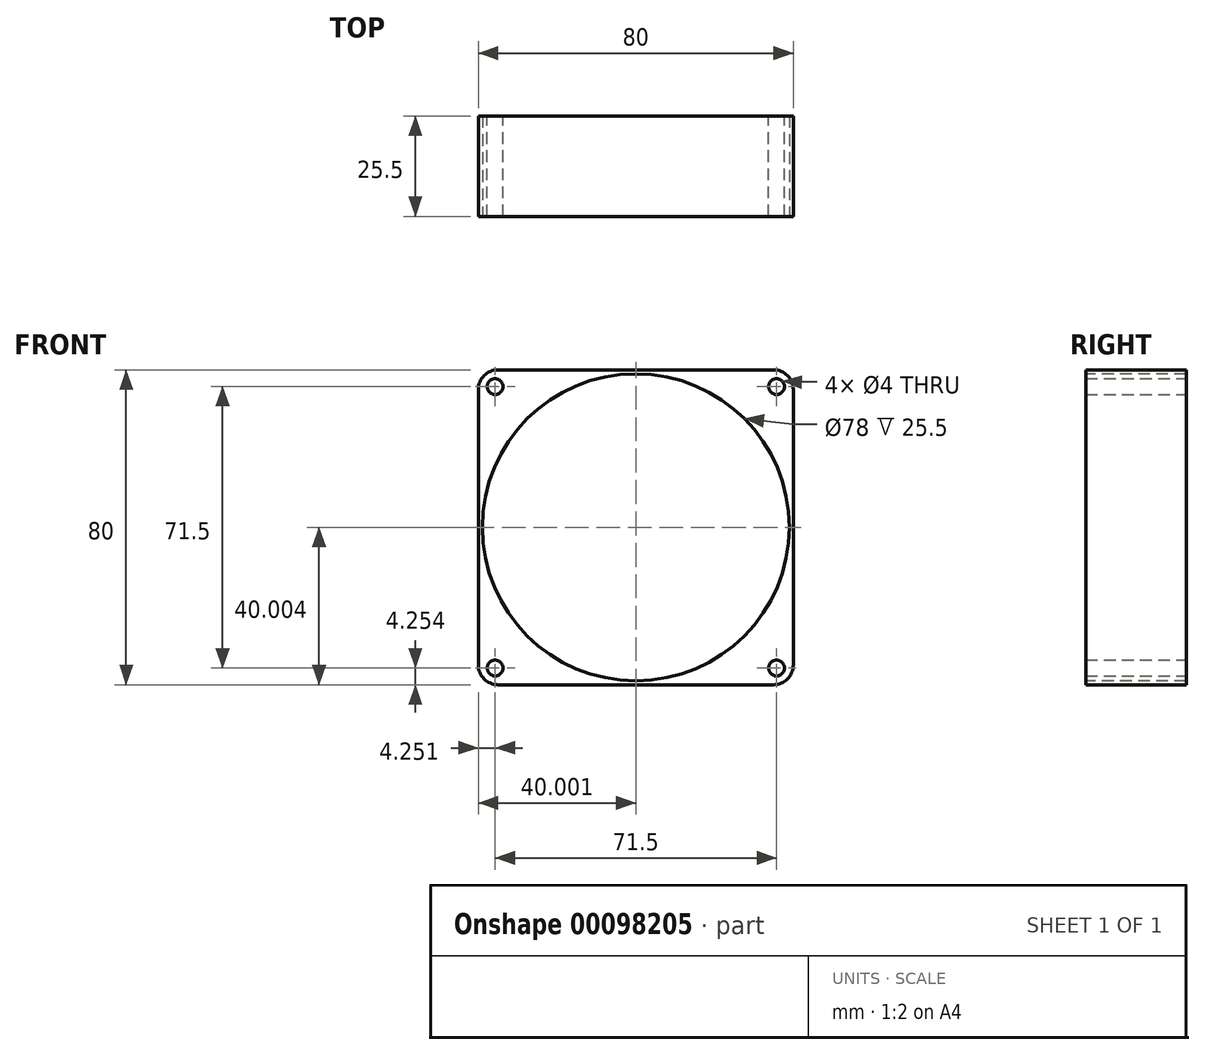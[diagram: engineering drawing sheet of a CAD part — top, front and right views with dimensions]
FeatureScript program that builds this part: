
annotation { "Feature Type Name" : "Feature", "Feature Type Description" : "" }
export const myFeature = defineFeature(function(context is Context, id is Id, definition is map)
    precondition{}
    {
        {
            var Q0;
            Q0=qCreatedBy(makeId("Front.planeOp"),FACE);
            var sketch = newSketch(context, id + "F0", { "sketchPlane" : qUnion([Q0])});
            skLineSegment(sketch, "E0.bottom", {"start": v(38.06, 38.5) * mm, "end": v(118.06, 38.5) * mm});
            skLineSegment(sketch, "E0.top", {"start": v(38.06, -41.5) * mm, "end": v(118.06, -41.5) * mm});
            skLineSegment(sketch, "E0.left", {"start": v(38.06, 38.5) * mm, "end": v(38.06, -41.5) * mm});
            skLineSegment(sketch, "E0.right", {"start": v(118.06, 38.5) * mm, "end": v(118.06, -41.5) * mm});
            skLineSegment(sketch, "E1", {"start": v(38.06, 34.24) * mm, "end": v(118.06, 34.24) * mm, "construction": true});
            skLineSegment(sketch, "E2", {"start": v(42.31, 38.5) * mm, "end": v(42.31, -41.5) * mm, "construction": true});
            skCircle(sketch, "E3", {"center": v(42.31, 34.24) * mm, "radius": 2 * mm});
            skCircle(sketch, "E4.0.1.0", {"center": v(42.31, -37.26) * mm, "radius": 2 * mm});
            skCircle(sketch, "E4.1.0.0", {"center": v(113.81, 34.24) * mm, "radius": 2 * mm});
            skCircle(sketch, "E4.1.1.0", {"center": v(113.81, -37.26) * mm, "radius": 2 * mm});
            skLineSegment(sketch, "E4.direction1", {"start": v(42.31, 34.24) * mm, "end": v(113.81, 34.24) * mm, "construction": true});
            skLineSegment(sketch, "E4.direction2", {"start": v(42.31, 34.24) * mm, "end": v(42.31, -37.26) * mm, "construction": true});
            skSolve(sketch);
        }
        {
            var Q0;
            Q0 = qSketchRegion(id + "F0", true);
            extrude(context, id + "F1", {"entities" : qUnion([Q0]), "depth" : 25.5 * mm});
        }
        {
            var Q0;
            Q0=makeQuery(id+"F1.opExtrude","SWEPT_EDGE",EDGE,{"disambiguationData":[OSD([sQuery(id+"F0.wireOp",EDGE,"E0.bottom"),sQuery(id+"F0.wireOp",EDGE,"E0.left")])]});
            var Q1;
            Q1=makeQuery(id+"F1.opExtrude","SWEPT_EDGE",EDGE,{"disambiguationData":[OSD([sQuery(id+"F0.wireOp",EDGE,"E0.top"),sQuery(id+"F0.wireOp",EDGE,"E0.left")])]});
            var Q2;
            Q2=makeQuery(id+"F1.opExtrude","SWEPT_EDGE",EDGE,{"disambiguationData":[OSD([sQuery(id+"F0.wireOp",EDGE,"E0.top"),sQuery(id+"F0.wireOp",EDGE,"E0.right")])]});
            var Q3;
            Q3=makeQuery(id+"F1.opExtrude","SWEPT_EDGE",EDGE,{"disambiguationData":[OSD([sQuery(id+"F0.wireOp",EDGE,"E0.bottom"),sQuery(id+"F0.wireOp",EDGE,"E0.right")])]});
            fillet(context, id + "F2", {"entities" : qUnion([Q0, Q1, Q2, Q3]), "radius" : 5 * mm, "tangentPropagation" : true, "allowEdgeOverflow" : false});
        }
        {
            var Q0;
            Q0=makeQuery(id+"F1.opExtrude","CAP_FACE",FACE,{"disambiguationData":[OSD([sQuery(id+"F0.wireOp",EDGE,"E0.bottom"),sQuery(id+"F0.wireOp",EDGE,"E0.top"),sQuery(id+"F0.wireOp",EDGE,"E0.left"),sQuery(id+"F0.wireOp",EDGE,"E0.right"),sQuery(id+"F0.wireOp",EDGE,"E3"),sQuery(id+"F0.wireOp",EDGE,"E4.0.1.0"),sQuery(id+"F0.wireOp",EDGE,"E4.1.0.0"),sQuery(id+"F0.wireOp",EDGE,"E4.1.1.0")])],"isStart":false});
            var sketch = newSketch(context, id + "F3", { "sketchPlane" : qUnion([Q0])});
            skLineSegment(sketch, "E5.0", {"start": v(38.06, 33.5) * mm, "end": v(38.06, -36.5) * mm});
            skLineSegment(sketch, "E6.0", {"start": v(43.06, 38.5) * mm, "end": v(113.06, 38.5) * mm});
            skPoint(sketch, "E7", {"position": v(78.06, 38.5) * mm});
            skPoint(sketch, "E8", {"position": v(38.06, -1.5) * mm});
            skCircle(sketch, "E9", {"center": v(78.06, -1.5) * mm, "radius": 39 * mm});
            skSolve(sketch);
        }
        {
            var Q0;
            Q0 = qSketchRegion(id + "F3", true);
            extrude(context, id + "F4", {"entities" : qUnion([Q0]), "operationType" : NewBodyOperationType.REMOVE, "endBound" : BoundingType.UP_TO_NEXT, "oppositeDirection" : true, "depth" : 25 * mm});
        }
    });
